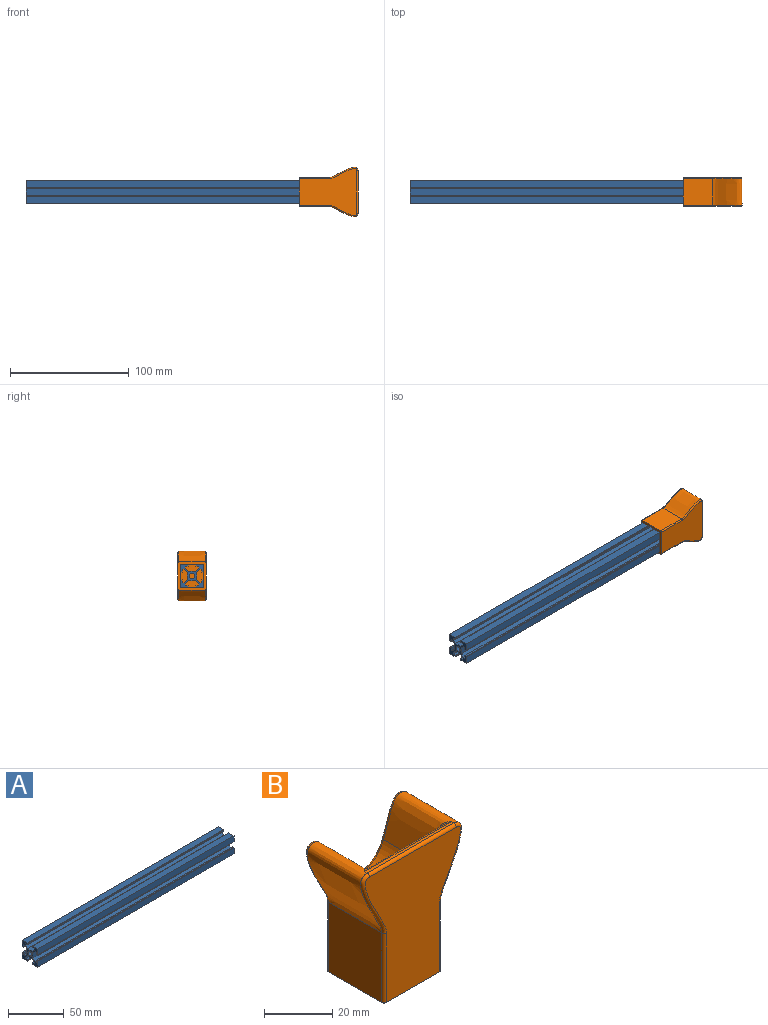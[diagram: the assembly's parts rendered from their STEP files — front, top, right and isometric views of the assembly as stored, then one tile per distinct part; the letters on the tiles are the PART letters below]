
ASSEMBLY  parts=2 mates=1
PART A: 63 faces, bbox 250x20x20 mm
  f0: plane 250x1.64mm, normal (0,0,-1), area 409.8mm2, adj f1,f59,f61,f62
  f1: plane 250x2.5mm, normal (0,-1,0), area 625mm2, adj f0,f2,f61,f62
  f2: plane 250x1.3mm, normal (0,0,-1), area 325mm2, adj f1,f3,f61,f62
  f3: plane 250x0.5mm, normal (0,1,0), area 125mm2, adj f2,f4,f61,f62
  f4: plane 250x0.5mm, normal (0,0,-1), area 125mm2, adj f3,f5,f61,f62
  f5: plane 250x6.5mm, normal (0,1,0), area 1625mm2, adj f4,f6,f61,f62
  f6: plane 250x6.5mm, normal (0,0,1), area 1625mm2, adj f5,f7,f61,f62
  f7: plane 250x0.5mm, normal (0,-1,0), area 125mm2, adj f6,f8,f61,f62
  f8: plane 250x0.5mm, normal (0,0,1), area 125mm2, adj f7,f9,f61,f62
  f9: plane 250x1.3mm, normal (0,-1,0), area 325mm2, adj f8,f10,f61,f62
  f10: plane 250x2.5mm, normal (0,0,-1), area 625mm2, adj f9,f11,f61,f62
  f11: plane 250x1.64mm, normal (0,-1,0), area 409.8mm2, adj f10,f12,f61,f62
  f12: plane 250x2.56mm, normal (0,-0.71,0.71), area 905.3mm2, adj f11,f13,f61,f62
  f13: plane 250x5.88mm, normal (0,0,1), area 1469.7mm2, adj f12,f14,f61,f62
  f14: plane 250x2.56mm, normal (0,0.71,0.71), area 905.3mm2, adj f13,f15,f61,f62
  f15: plane 250x1.64mm, normal (0,1,0), area 409.8mm2, adj f14,f16,f61,f62
  f16: plane 250x2.5mm, normal (0,0,-1), area 625mm2, adj f15,f17,f61,f62
  f17: plane 250x1.3mm, normal (0,1,0), area 325mm2, adj f16,f18,f61,f62
  f18: plane 250x0.5mm, normal (0,0,1), area 125mm2, adj f17,f19,f61,f62
  f19: plane 250x0.5mm, normal (0,1,0), area 125mm2, adj f18,f20,f61,f62
  f20: plane 250x6.5mm, normal (0,0,1), area 1625mm2, adj f19,f21,f61,f62
  f21: plane 250x6.5mm, normal (0,-1,0), area 1625mm2, adj f20,f22,f61,f62
  f22: plane 250x0.5mm, normal (0,0,-1), area 125mm2, adj f21,f23,f61,f62
  f23: plane 250x0.5mm, normal (0,-1,0), area 125mm2, adj f22,f24,f61,f62
  f24: plane 250x1.3mm, normal (0,0,-1), area 325mm2, adj f23,f25,f61,f62
  f25: plane 250x2.5mm, normal (0,1,0), area 625mm2, adj f24,f26,f61,f62
  f26: plane 250x1.64mm, normal (0,0,-1), area 409.8mm2, adj f25,f27,f61,f62
  f27: plane 250x2.56mm, normal (0,-0.71,-0.71), area 905.3mm2, adj f26,f28,f61,f62
  f28: plane 250x5.88mm, normal (0,-1,0), area 1469.7mm2, adj f27,f29,f61,f62
  f29: plane 250x2.56mm, normal (0,-0.71,0.71), area 905.3mm2, adj f28,f30,f61,f62
  f30: plane 250x1.64mm, normal (0,0,1), area 409.8mm2, adj f29,f31,f61,f62
  f31: plane 250x2.5mm, normal (0,1,0), area 625mm2, adj f30,f32,f61,f62
  f32: plane 250x1.3mm, normal (0,0,1), area 325mm2, adj f31,f33,f61,f62
  f33: plane 250x0.5mm, normal (0,-1,0), area 125mm2, adj f32,f34,f61,f62
  f34: plane 250x0.5mm, normal (0,0,1), area 125mm2, adj f33,f35,f61,f62
  f35: plane 250x6.5mm, normal (0,-1,0), area 1625mm2, adj f34,f36,f61,f62
  f36: plane 250x6.5mm, normal (0,0,-1), area 1625mm2, adj f35,f37,f61,f62
  f37: plane 250x0.5mm, normal (0,1,0), area 125mm2, adj f36,f38,f61,f62
  f38: plane 250x0.5mm, normal (0,0,-1), area 125mm2, adj f37,f39,f61,f62
  f39: plane 250x1.3mm, normal (0,1,0), area 325mm2, adj f38,f40,f61,f62
  f40: plane 250x2.5mm, normal (0,0,1), area 625mm2, adj f39,f41,f61,f62
  f41: plane 250x1.64mm, normal (0,1,0), area 409.8mm2, adj f40,f42,f61,f62
  f42: plane 250x2.56mm, normal (0,0.71,-0.71), area 905.3mm2, adj f41,f43,f61,f62
  f43: plane 250x5.88mm, normal (0,0,-1), area 1469.7mm2, adj f42,f44,f61,f62
  f44: plane 250x2.56mm, normal (0,-0.71,-0.71), area 905.3mm2, adj f43,f45,f61,f62
  f45: plane 250x1.64mm, normal (0,-1,0), area 409.8mm2, adj f44,f46,f61,f62
  f46: plane 250x2.5mm, normal (0,0,1), area 625mm2, adj f45,f47,f61,f62
  f47: plane 250x1.3mm, normal (0,-1,0), area 325mm2, adj f46,f48,f61,f62
  f48: plane 250x0.5mm, normal (0,0,-1), area 125mm2, adj f47,f49,f61,f62
  f49: plane 250x0.5mm, normal (0,-1,0), area 125mm2, adj f48,f50,f61,f62
  f50: plane 250x6.5mm, normal (0,0,-1), area 1625mm2, adj f49,f51,f61,f62
  f51: plane 250x6.5mm, normal (0,1,0), area 1625mm2, adj f50,f52,f61,f62
  f52: plane 250x0.5mm, normal (0,0,1), area 125mm2, adj f51,f53,f61,f62
  f53: plane 250x0.5mm, normal (0,1,0), area 125mm2, adj f52,f54,f61,f62
  f54: plane 250x1.3mm, normal (0,0,1), area 325mm2, adj f53,f55,f61,f62
  f55: plane 250x2.5mm, normal (0,-1,0), area 625mm2, adj f54,f56,f61,f62
  f56: plane 250x1.64mm, normal (0,0,1), area 409.8mm2, adj f55,f57,f61,f62
  f57: plane 250x2.56mm, normal (0,0.71,0.71), area 905.3mm2, adj f56,f58,f61,f62
  f58: plane 250x5.88mm, normal (0,1,0), area 1469.7mm2, adj f57,f59,f61,f62
  f59: plane 250x2.56mm, normal (0,0.71,-0.71), area 905.3mm2, adj f0,f58,f61,f62
  f60: cylinder r=2.4mm len=250mm, axis (-1,0,0), area 3769.9mm2, adj f61,f62
  f61: plane 20x20mm, normal (1,0,0), area 178.1mm2, adj f0,f1,f2,f3,f4,f5,f6,f7
  f62: plane 20x20mm, normal (-1,0,0), area 178.1mm2, adj f0,f1,f2,f3,f4,f5,f6,f7
PART B: 31 faces, bbox 41.5x24x49.5 mm
  f0: extruded ~24.52x22mm, area 921.3mm2, adj f1,f4,f13,f16,f22,f24,f27
  f1: cylinder r=11.5mm len=21.63mm, axis (0,1,0), area 535.1mm2, adj f0,f2,f25,f28
  f2: extruded ~24.52x22mm, area 921.3mm2, adj f1,f5,f13,f19,f21,f23,f29
  f3: plane 24x24mm, normal (0,0,-1), area 175.1mm2, adj f4,f5,f6,f7,f8,f9,f10,f11
  f4: plane 25x22mm, normal (1,0,0), area 550mm2, adj f0,f3,f15,f26
  f5: plane 25x22mm, normal (-1,0,0), area 550mm2, adj f2,f3,f18,f30
  f6: plane 48.52x39.51mm, normal (0,-1,0), area 1297.8mm2, adj f3,f15,f16,f17,f18,f19
  f7: plane 48.52x39.51mm, normal (0,1,0), area 797.6mm2, adj f3,f26,f27,f28,f29,f30
  f8: plane 20x20mm, normal (0,-1,0), area 400mm2, adj f3,f9,f11,f12
  f9: plane 20x20mm, normal (-1,0,0), area 400mm2, adj f3,f8,f10,f12
  f10: plane 20x20mm, normal (0,1,0), area 400mm2, adj f3,f9,f11,f12
  f11: plane 20x20mm, normal (1,0,0), area 400mm2, adj f3,f8,f10,f12
  f12: plane 20x20mm, normal (0,0,-1), area 400mm2, adj f8,f9,f10,f11
  f13: plane 35.96x1mm, normal (0,0,1), area 36mm2, adj f0,f2,f17,f20
  f14: plane 29.25x19.02mm, normal (0,1,0), area 390mm2, adj f20,f23,f24,f25
  f15: cylinder r=1mm len=25mm, axis (0,0,-1), area 39.3mm2, adj f3,f4,f6,f16
  f16: bspline ~24.66x9.76mm, area 43.2mm2, adj f0,f6,f15,f17
  f17: cylinder r=1mm len=35.96mm, axis (-1,0,0), area 56.5mm2, adj f6,f13,f16,f19
  f18: cylinder r=1mm len=25mm, axis (0,0,1), area 39.3mm2, adj f3,f5,f6,f19
  f19: bspline ~24.66x9.76mm, area 43.2mm2, adj f2,f6,f17,f18
  f20: cylinder r=1mm len=35.96mm, axis (1,0,0), area 51.2mm2, adj f13,f14,f21,f22
  f21: bspline ~3.73x2.08mm, area 1.9mm2, adj f2,f20,f23
  f22: bspline ~3.73x2.08mm, area 1.9mm2, adj f0,f20,f24
  f23: bspline ~14.55x6.41mm, area 20.2mm2, adj f2,f14,f21,f25
  f24: bspline ~14.55x6.41mm, area 20.2mm2, adj f0,f14,f22,f25
  f25: torus R=10.5mm, axis (0,-1,0), area 42.8mm2, adj f1,f14,f23,f24
  f26: cylinder r=1mm len=25mm, axis (0,0,1), area 39.3mm2, adj f3,f4,f7,f27
  f27: bspline ~24.63x10.34mm, area 67.4mm2, adj f0,f7,f26,f28
  f28: torus R=12.5mm, axis (0,-1,0), area 45.6mm2, adj f1,f7,f27,f29
  f29: bspline ~24.8x10.34mm, area 67.4mm2, adj f2,f7,f28,f30
  f30: cylinder r=1mm len=25mm, axis (0,0,-1), area 39.3mm2, adj f3,f5,f7,f29
PLACE A t=(33.81,61.61,-12.83)mm
PLACE B rot(axis=(0,1,0),90deg) t=(138.81,61.61,-12.83)mm
MATE fastened A.f60 <-> B.f12  axis (1,0,0) through (158.81,61.61,-12.83)mm
